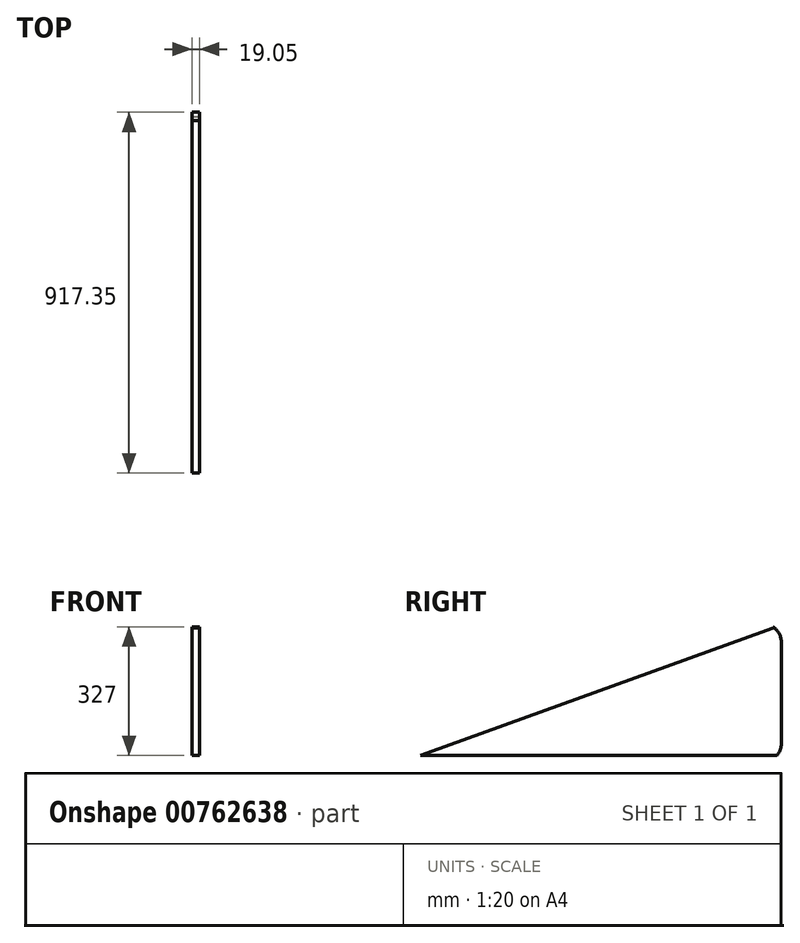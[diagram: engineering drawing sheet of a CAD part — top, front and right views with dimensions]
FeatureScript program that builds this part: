
annotation { "Feature Type Name" : "Feature", "Feature Type Description" : "" }
export const myFeature = defineFeature(function(context is Context, id is Id, definition is map)
    precondition{}
    {
        {
            var Q0;
            Q0=qCreatedBy(makeId("Right.planeOp"),FACE);
            var sketch = newSketch(context, id + "F0", { "sketchPlane" : qUnion([Q0])});
            skLineSegment(sketch, "E0.bottom", {"start": v(-482.6, 177.8) * mm, "end": v(482.6, 177.8) * mm});
            skLineSegment(sketch, "E0.top", {"start": v(-482.6, -177.8) * mm, "end": v(482.6, -177.8) * mm});
            skLineSegment(sketch, "E0.left", {"start": v(-482.6, 177.8) * mm, "end": v(-482.6, -177.8) * mm});
            skLineSegment(sketch, "E0.right", {"start": v(482.6, 177.8) * mm, "end": v(482.6, -177.8) * mm});
            skPoint(sketch, "E0.middle", {"position": v(0, 0) * mm});
            skLineSegment(sketch, "E1", {"start": v(482.6, 177.8) * mm, "end": v(431.8, 177.8) * mm});
            skLineSegment(sketch, "E2", {"start": v(431.8, 177.8) * mm, "end": v(431.8, 127) * mm});
            skLineSegment(sketch, "E3", {"start": v(482.6, -177.8) * mm, "end": v(482.6, -127) * mm});
            skLineSegment(sketch, "E4", {"start": v(482.6, -127) * mm, "end": v(431.8, -127) * mm});
            skLineSegment(sketch, "E5", {"start": v(-482.6, -177.8) * mm, "end": v(-482.6, -152.4) * mm});
            skLineSegment(sketch, "E6", {"start": v(431.8, 177.8) * mm, "end": v(-482.6, -152.4) * mm});
            skArc(sketch, "E7", {"start": v(431.8, 177.8) * mm, "mid": v(467.72, 162.92) * mm, "end": v(482.6, 127) * mm});
            skArc(sketch, "E8", {"start": v(482.6, -127) * mm, "mid": v(467.72, -162.92) * mm, "end": v(431.8, -177.8) * mm});
            skLineSegment(sketch, "E9", {"start": v(-482.6, -177.8) * mm, "end": v(-457.2, -177.8) * mm});
            skLineSegment(sketch, "E10", {"start": v(-457.2, -177.8) * mm, "end": v(-457.2, -152.4) * mm});
            skArc(sketch, "E11", {"start": v(-482.6, -152.4) * mm, "mid": v(-475.16, -170.36) * mm, "end": v(-457.2, -177.8) * mm});
            skSolve(sketch);
        }
        {
            var Q0;
            Q0=makeQuery(id+"F0.imprint","IMPRINT",FACE,{"disambiguationData":[TD([[makeQuery(id+"F0.imprint","IMPRINT",EDGE,{"derivedFrom":sQuery(id+"F0.wireOp",EDGE,"E6")}),1.0]])]});
            extrude(context, id + "F1", {"entities" : qUnion([Q0]), "depth" : 19.05 * mm, "offsetDistance" : 25.4 * mm});
        }
        {
            var Q0;
            Q0=makeQuery(id+"F1.opExtrude","CAP_FACE",FACE,{"disambiguationData":[OSD([sQuery(id+"F0.wireOp",EDGE,"E0.top"),sQuery(id+"F0.wireOp",EDGE,"E0.right"),sQuery(id+"F0.wireOp",EDGE,"E6"),sQuery(id+"F0.wireOp",EDGE,"E7"),sQuery(id+"F0.wireOp",EDGE,"E8"),sQuery(id+"F0.wireOp",EDGE,"E11")])],"isStart":false});
            var sketch = newSketch(context, id + "F2", { "sketchPlane" : qUnion([Q0])});
            skLineSegment(sketch, "E12", {"start": v(-25.4, 12.7) * mm, "end": v(-18.93, -5.22) * mm});
            skLineSegment(sketch, "E13", {"start": v(-18.93, -5.22) * mm, "end": v(461.45, 168.25) * mm});
            skLineSegment(sketch, "E14", {"start": v(-18.93, -5.22) * mm, "end": v(-475.45, -170.07) * mm});
            skLineSegment(sketch, "E15", {"start": v(-12.7, -177.8) * mm, "end": v(-12.7, -158.75) * mm});
            skLineSegment(sketch, "E16", {"start": v(-12.7, -158.75) * mm, "end": v(-444.1, -158.75) * mm});
            skLineSegment(sketch, "E17", {"start": v(-12.7, -158.75) * mm, "end": v(471.46, -158.75) * mm});
            skLineSegment(sketch, "E18", {"start": v(471.46, -158.75) * mm, "end": v(433.36, -158.75) * mm});
            skLineSegment(sketch, "E19", {"start": v(433.36, -158.75) * mm, "end": v(433.36, 158.1) * mm});
            skSolve(sketch);
        }
        {
            var Q0;
            {var subQ2=sQuery(id+"F2.wireOp",EDGE,"E18");Q0=makeQuery(id+"F2.imprint","IMPRINT",FACE,{"disambiguationData":[TD([[makeQuery(id+"F2.imprint","IMPRINT",EDGE,{"derivedFrom":subQ2}),-1.0]])]});}
            var Q1;
            {var subQ3=sQuery(id+"F2.wireOp",EDGE,"E12");Q1=makeQuery(id+"F2.imprint","IMPRINT",FACE,{"disambiguationData":[TD([[makeQuery(id+"F2.imprint","IMPRINT",EDGE,{"derivedFrom":subQ3}),1.0]])]});}
            var Q2;
            {var subQ3=sQuery(id+"F2.wireOp",EDGE,"E12");Q2=makeQuery(id+"F2.imprint","IMPRINT",FACE,{"disambiguationData":[TD([[makeQuery(id+"F2.imprint","IMPRINT",EDGE,{"derivedFrom":subQ3}),-1.0]])]});}
            var Q3;
            {var subQ3=sQuery(id+"F2.wireOp",EDGE,"E15");Q3=makeQuery(id+"F2.imprint","IMPRINT",FACE,{"disambiguationData":[TD([[makeQuery(id+"F2.imprint","IMPRINT",EDGE,{"derivedFrom":subQ3}),1.0]])]});}
            var Q4;
            {var subQ4=sQuery(id+"F2.wireOp",EDGE,"E15");Q4=makeQuery(id+"F2.imprint","IMPRINT",FACE,{"disambiguationData":[TD([[makeQuery(id+"F2.imprint","IMPRINT",EDGE,{"derivedFrom":subQ4}),-1.0]])]});}
            extrude(context, id + "F3", {"entities" : qUnion([Q0, Q1, Q2, Q3, Q4]), "operationType" : NewBodyOperationType.REMOVE, "oppositeDirection" : true, "depth" : 25.4 * mm, "offsetDistance" : 25.4 * mm});
        }
        {
            var Q0;
            Q0=makeQuery(id+"F3.boolean.opBoolean","COPY",FACE,{"derivedFrom":makeQuery(id+"F3.opExtrude","SWEPT_FACE",FACE,{"disambiguationData":[OSD([sQuery(id+"F2.wireOp",EDGE,"E13"),sQuery(id+"F2.wireOp",EDGE,"E14")])]})});
            extrude(context, id + "F4", {"entities" : qUnion([Q0]), "operationType" : NewBodyOperationType.REMOVE, "oppositeDirection" : true, "depth" : 3.17 * mm, "offsetDistance" : 25.4 * mm});
        }
    });
